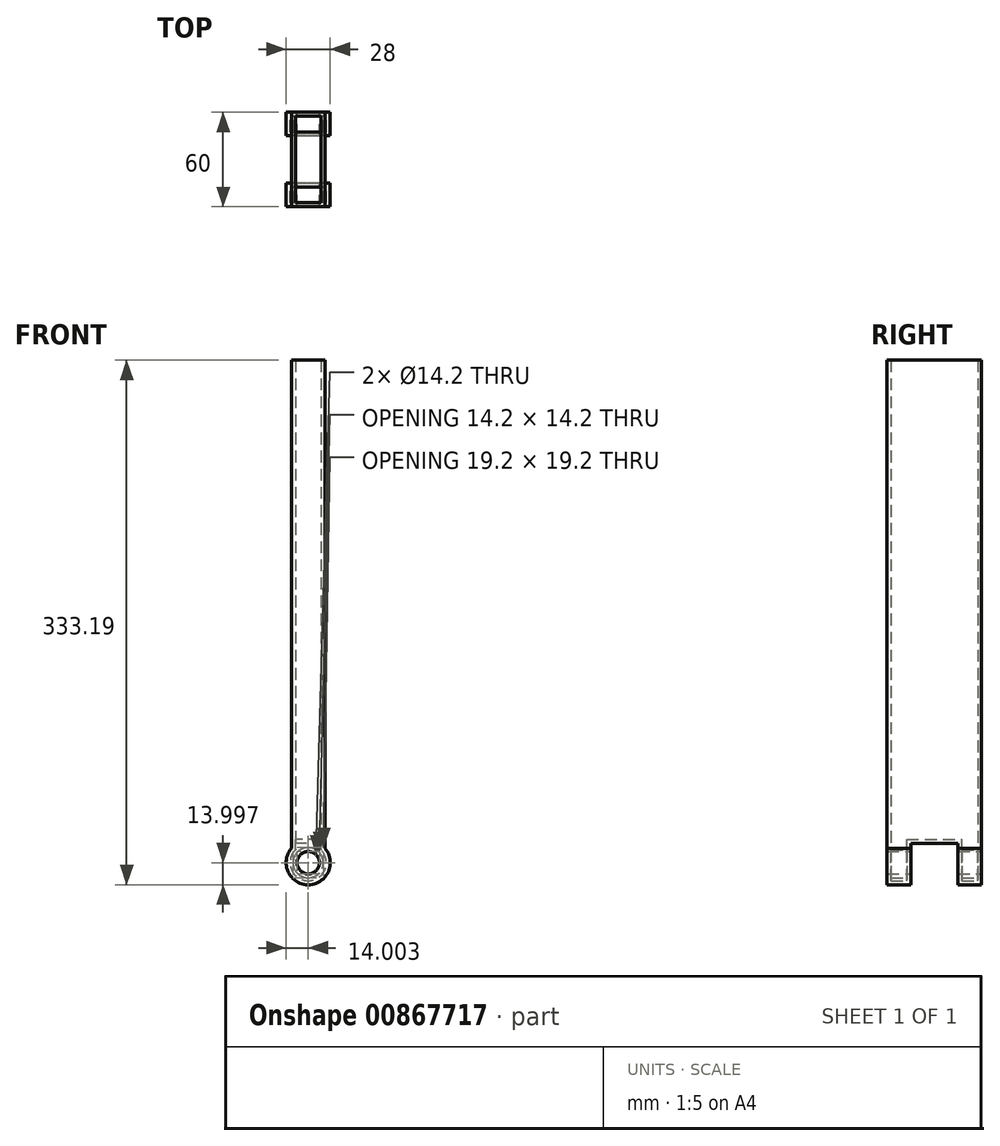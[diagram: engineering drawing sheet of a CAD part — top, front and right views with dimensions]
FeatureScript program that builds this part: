
annotation { "Feature Type Name" : "Feature", "Feature Type Description" : "" }
export const myFeature = defineFeature(function(context is Context, id is Id, definition is map)
    precondition{}
    {
        {
            var Q0;
            Q0=qCreatedBy(makeId("Front.planeOp"),FACE);
            var sketch = newSketch(context, id + "F0", { "sketchPlane" : qUnion([Q0])});
            skCircle(sketch, "E0", {"center": v(-44.98, -84.28) * mm, "radius": 7.1 * mm});
            skArc(sketch, "E1", {"start": v(-55.54, -75.09) * mm, "mid": v(-44.98, -98.28) * mm, "end": v(-34.42, -75.1) * mm});
            skLineSegment(sketch, "E2.bottom", {"start": v(-55.54, 234.91) * mm, "end": v(-34.42, 234.9) * mm});
            skLineSegment(sketch, "E2.left", {"start": v(-55.54, 234.91) * mm, "end": v(-55.54, -75.09) * mm});
            skLineSegment(sketch, "E2.right", {"start": v(-34.42, 234.9) * mm, "end": v(-34.42, -75.1) * mm});
            skPoint(sketch, "E2.middle", {"position": v(-44.98, 79.9) * mm});
            skSolve(sketch);
        }
        {
            var Q0;
            Q0=makeQuery(id+"F0.imprint","IMPRINT",FACE,{"disambiguationData":[TD([[makeQuery(id+"F0.imprint","IMPRINT",EDGE,{"derivedFrom":sQuery(id+"F0.wireOp",EDGE,"E0")}),-1.0]])]});
            extrude(context, id + "F1", {"entities" : qUnion([Q0]), "depth" : 60 * mm, "offsetDistance" : 25 * mm});
        }
        {
            var Q0;
            Q0=makeQuery(id+"F1.opExtrude","SWEPT_FACE",FACE,{"disambiguationData":[OSD([sQuery(id+"F0.wireOp",EDGE,"E2.left")])]});
            var sketch = newSketch(context, id + "F2", { "sketchPlane" : qUnion([Q0])});
            skLineSegment(sketch, "E3.bottom", {"start": v(15, -71.9) * mm, "end": v(45, -71.9) * mm});
            skLineSegment(sketch, "E3.top", {"start": v(15, -104.14) * mm, "end": v(45, -104.14) * mm});
            skLineSegment(sketch, "E3.left", {"start": v(15, -71.9) * mm, "end": v(15, -104.14) * mm});
            skLineSegment(sketch, "E3.right", {"start": v(45, -71.9) * mm, "end": v(45, -104.14) * mm});
            skSolve(sketch);
        }
        {
            var Q0;
            Q0 = qSketchRegion(id + "F2", true);
            extrude(context, id + "F3", {"entities" : qUnion([Q0]), "operationType" : NewBodyOperationType.REMOVE, "oppositeDirection" : true, "depth" : 25 * mm, "offsetDistance" : 25 * mm, "hasSecondDirection" : true, "secondDirectionOppositeDirection" : false, "secondDirectionDepth" : 25 * mm});
        }
        {
            var Q0;
            Q0=makeQuery(id+"F1.opExtrude","SWEPT_FACE",FACE,{"disambiguationData":[OSD([sQuery(id+"F0.wireOp",EDGE,"E2.bottom")])]});
            shell(context, id + "F4", {"entities" : qUnion([Q0]), "thickness" : 2.5 * mm});
        }
    });
